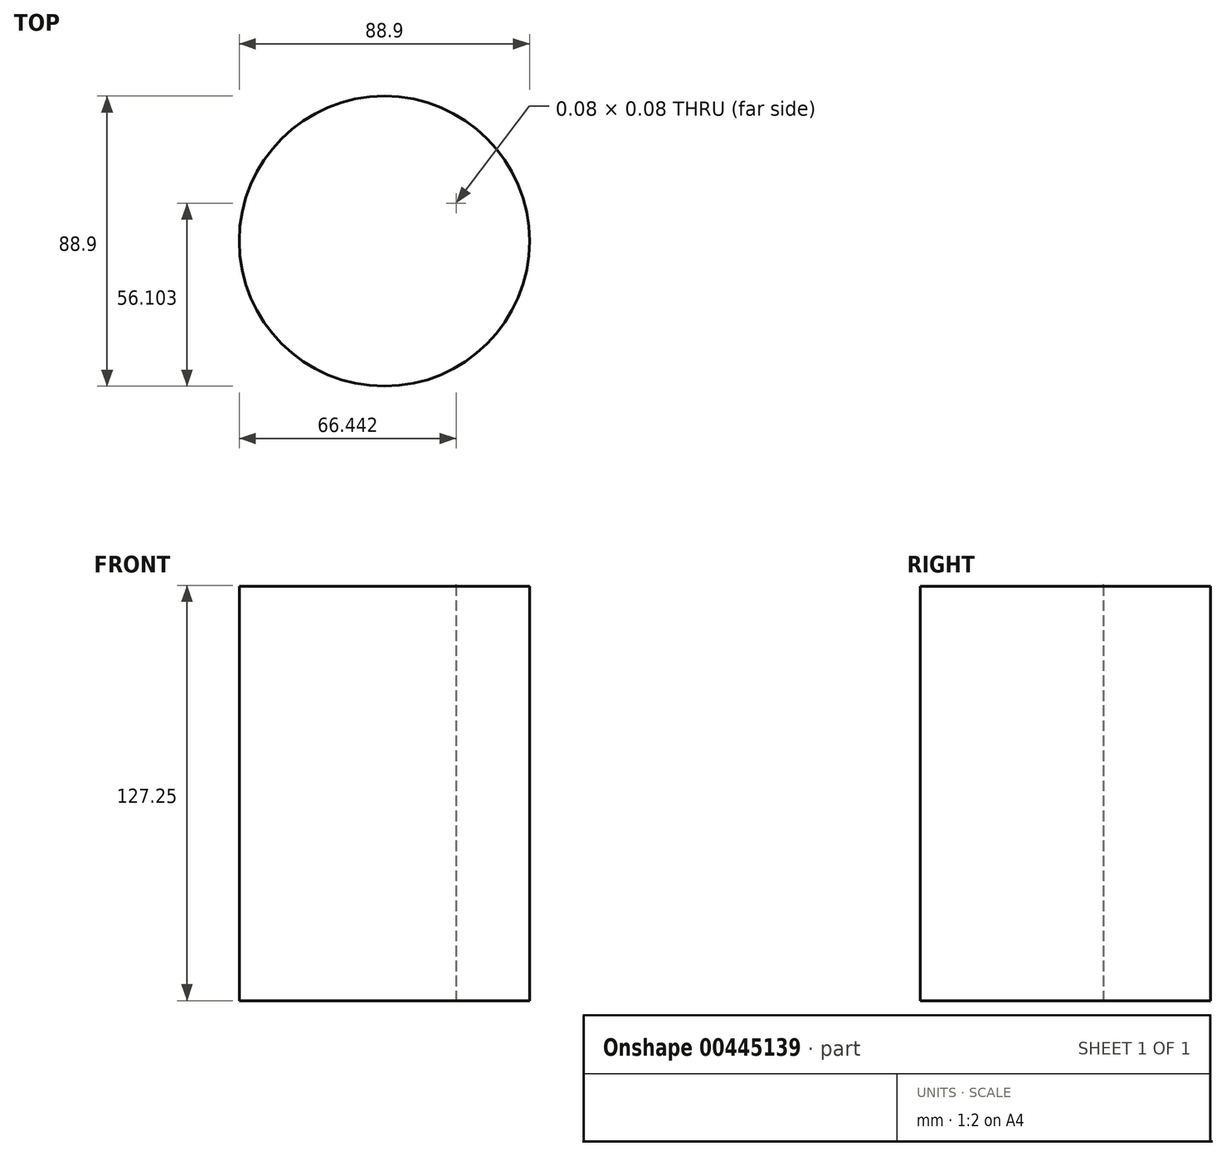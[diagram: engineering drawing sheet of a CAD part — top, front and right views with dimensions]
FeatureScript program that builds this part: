
annotation { "Feature Type Name" : "Feature", "Feature Type Description" : "" }
export const myFeature = defineFeature(function(context is Context, id is Id, definition is map)
    precondition{}
    {
        {
            var Q0;
            Q0=qCreatedBy(makeId("Top.planeOp"),FACE);
            var sketch = newSketch(context, id + "F0", { "sketchPlane" : qUnion([Q0])});
            skCircle(sketch, "E0", {"center": v(0, 0) * mm, "radius": 44.45 * mm});
            skLineSegment(sketch, "E1.bottom", {"start": v(21.95, 11.7) * mm, "end": v(22.03, 11.7) * mm});
            skLineSegment(sketch, "E1.top", {"start": v(21.95, 11.62) * mm, "end": v(22.03, 11.62) * mm});
            skLineSegment(sketch, "E1.left", {"start": v(21.95, 11.7) * mm, "end": v(21.95, 11.62) * mm});
            skLineSegment(sketch, "E1.right", {"start": v(22.03, 11.7) * mm, "end": v(22.03, 11.62) * mm});
            skSolve(sketch);
        }
        {
            var Q0;
            Q0=makeQuery(id+"F0.imprint","IMPRINT",FACE,{"disambiguationData":[TD([[makeQuery(id+"F0.imprint","IMPRINT",EDGE,{"derivedFrom":sQuery(id+"F0.wireOp",EDGE,"E0")}),1.0]])]});
            extrude(context, id + "F1", {"entities" : qUnion([Q0]), "depth" : 127 * mm});
        }
        {
            var Q0;
            Q0=makeQuery(id+"F0.imprint","IMPRINT",FACE,{"disambiguationData":[TD([[makeQuery(id+"F0.imprint","IMPRINT",EDGE,{"derivedFrom":sQuery(id+"F0.wireOp",EDGE,"E1.bottom")}),-1.0]])]});
            extrude(context, id + "F2", {"entities" : qUnion([Q0]), "depth" : 127.25 * mm});
        }
    });
